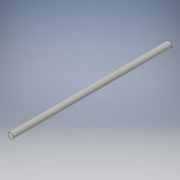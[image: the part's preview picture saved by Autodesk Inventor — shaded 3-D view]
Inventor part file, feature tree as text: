
AUTODESK INVENTOR PART (.ipt)
format: ipt  version: 2016 (Build 200138000, 138)  size: 86,528 bytes
history: native  units: in
note: dims shown in document units (in); Inventor stores cm internally (conversion verified against a paired STEP export)
features: extrude x1, sketch x1
ambient origin geometry x8: Origin, YZ Plane, XZ Plane, XY Plane, X Axis, Y Axis, Z Axis, Center Point
bodies: Solid1 (feature_tree)
feature tree (2):
  extrude  "Extrusion1"  Depth=14.0in TaperAngle=0.0deg
  sketch  "Sketch1"  dims[d0=0.5in d1=14.0in d2=0.0in]
